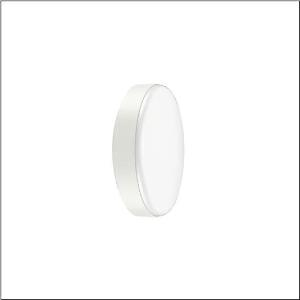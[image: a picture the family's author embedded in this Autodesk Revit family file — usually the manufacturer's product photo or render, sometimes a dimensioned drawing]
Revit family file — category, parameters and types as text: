
# Revit family: round_31_51wc10ma32as
name_source: partatom
category: Lighting Fixtures
units: mm (PartAtom-declared; Revit-internal decimal feet)

## family parameters
Cut with Voids When Loaded = No
Host = Face
Light Source = No
Part Type = Normal
Room Calculation Point = No
Round Connector Dimension = Use Diameter
Shared = No

## types (1)
- --- (1 x LED, 2450 lm, 20.4 W, 3000K)
    Apparent Load = 20 VA
    CIE Flux Codes = 44 75 94 94 100
    Color Rendering = 80
    Color Temperature = 3000K
    Default Elevation = 1800 mm
    Description = Round 31, wall and ceiling luminaire, primary optical cover: cover, of PC, opal, light emission: direct distribution, primary light characteristic: symmetric, installation type: surface-mounted, LED, rated luminous flux: 2.450lm, luminous efficacy: 120lm/W, light colour: 830, colour temperature: 3000K, control gear: ON/OFF Multilumen, with terminal, 3-pole, max. 2.5mm², mains connection: 220..240V, AC, 50/60Hz, rated input power: 20.5W, luminaire housing, of PC, traffic white (RAL 9016), diameter: 350mm, brightness and presence sensor, HF sensor, protection rating (complete): IP65, insulation class (complete): insulation class II (safety insulation), certification: CE, impact resistance: IK10, permissible operating ambient temperature: -20..+40°C, permissible storage temperature: -20..+60°C, packaging unit: 1 piece
    Height = 97 mm
    Lamp = 1 x LED
    Lamp Light Flux = 2450 lm
    Lamp Power = 20.4 W
    Lamp count = 1
    Length = 350 mm
    Luminous efficacy = 120 lm/W
    Manufacturer = Siteco
    ModVariant = No
    Model = 51WC10MA32AS
    Mounting Place = Wall
    Mounting Type = Surface mounted
    Number of Poles = 1
    OnlyDefault = Yes
    Power Factor = 1
    Product Name = Round 31
    Product group = wall and ceiling luminaire
    ProductGroupID = 2001
    Protection Class = Protection class II
    Protection Degree = IP 65
    RLX_Detail_Level = 1
    RLX_Emergency_Light_Flux = 0 lm
    RLX_Emergency_Type = 0
    RLX_Emergency_Type_DB = No
    RlxData = <blob elided: 30385 chars, md5=71dc9aac>
    Socket = socket
    Standby Power = 0 W
    System Light Flux = 2450 lm
    System Power = 20 W
    Type Comments = factory setting: luminous flux: 100 % | (ON | ON)
    Type Image = l_1007027.jpg
    URL = http://relux.com
    VarID = @adj_115763
    Voltage = 0 V
    Weight = 0.00 kg
    Width = 0 mm  [stored 0 ft]

note: [stored X ft] marks values corroborated as IEEE doubles in the binary element streams (Revit-internal decimal feet)

## geometry (parser evidence)
native form markers: Blend x4, Sweep x9
no freeform markers — native parametric forms only
